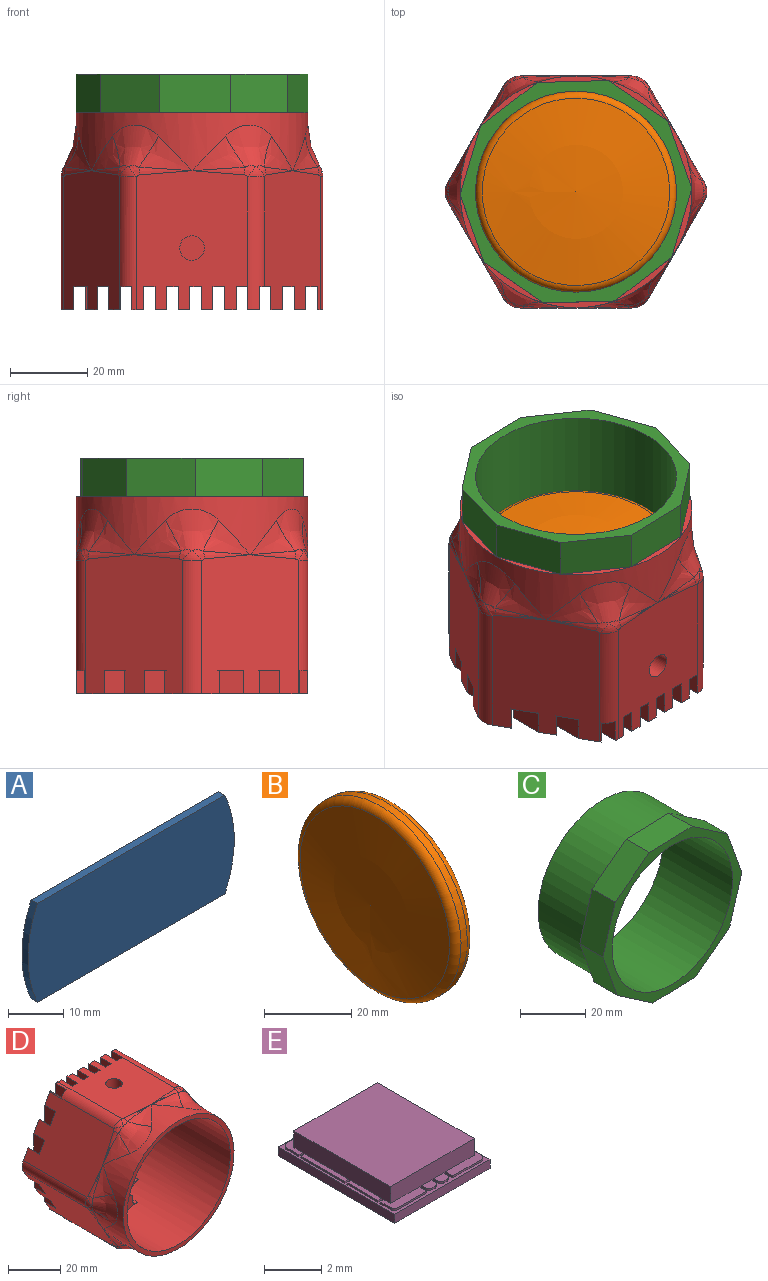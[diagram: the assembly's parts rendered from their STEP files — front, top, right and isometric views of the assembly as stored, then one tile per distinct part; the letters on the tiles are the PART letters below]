
ASSEMBLY  parts=5 mates=4
PART A: 6 faces, bbox 53x1.6x22 mm
  f0: plane 48.22x1.6mm, normal (0,0,1), area 77.1mm2, adj f1,f3,f4,f5
  f1: cylinder r=26.5mm len=22mm, axis (0,1,0), area 36.3mm2, adj f0,f2,f4,f5
  f2: plane 48.22x1.6mm, normal (0,0,-1), area 77.1mm2, adj f1,f3,f4,f5
  f3: cylinder r=26.5mm len=22mm, axis (0,1,0), area 36.3mm2, adj f0,f2,f4,f5
  f4: plane 53x22mm, normal (0,-1,0), area 1131.6mm2, adj f0,f1,f2,f3
  f5: plane 53x22mm, normal (0,1,0), area 1131.6mm2, adj f0,f1,f2,f3
PART B: 5 faces, bbox 11.1x56.3x56.3 mm
  f0: torus R=24mm, axis (1,0,0), area 463.2mm2, adj f1,f4
  f1: cylinder r=26mm len=52mm, axis (1,0,0), area 326.7mm2, adj f0,f2
  f2: torus R=24mm, axis (1,0,0), area 419.7mm2, adj f1,f3
  f3: sphere r=84.13mm, area 1929.7mm2, adj f2
  f4: sphere r=190.83mm, area 1852.7mm2, adj f0
PART C: 15 faces, bbox 60x30x57.5 mm
  f0: cylinder r=28mm len=56mm, axis (0,1,0), area 3518.6mm2, adj f3,f14
  f1: cylinder r=26mm len=52mm, axis (0,1,0), area 4900.9mm2, adj f2,f3
  f2: plane 59.98x57.54mm, normal (0,-1,0), area 521.3mm2, adj f1,f4,f5,f6,f7,f8,f9,f10
  f3: plane 56x56mm, normal (0,1,0), area 339.3mm2, adj f0,f1
  f4: plane 17.78x10mm, normal (0.96,0,-0.28), area 185.4mm2, adj f2,f5,f13,f14
  f5: plane 17.47x10mm, normal (0.94,0,0.33), area 185.4mm2, adj f2,f4,f6,f14
  f6: plane 15.29x10.49mm, normal (0.57,0,0.82), area 185.4mm2, adj f2,f5,f7,f14
  f7: plane 18.53x10mm, normal (-0.03,0,1), area 185.4mm2, adj f2,f6,f8,f14
  f8: plane 14.7x11.3mm, normal (-0.61,0,0.79), area 185.4mm2, adj f2,f7,f9,f14
  f9: plane 17.78x10mm, normal (-0.96,0,0.28), area 185.4mm2, adj f2,f8,f10,f14
  f10: plane 17.47x10mm, normal (-0.94,0,-0.33), area 185.4mm2, adj f2,f9,f11,f14
  f11: plane 15.29x10.49mm, normal (-0.57,0,-0.82), area 185.4mm2, adj f2,f10,f12,f14
  f12: plane 18.53x10mm, normal (0.03,0,-1), area 185.4mm2, adj f2,f11,f13,f14
  f13: plane 14.7x11.3mm, normal (0.61,0,-0.79), area 185.4mm2, adj f2,f4,f12,f14
  f14: plane 59.98x57.54mm, normal (0,1,0), area 182mm2, adj f0,f4,f5,f6,f7,f8,f9,f10
PART D: 168 faces, bbox 72x51.3x64.5 mm
  f0: plane 54.08x30.15mm, normal (0,-1,0), area 1184.2mm2, adj f7,f94,f95,f144,f145,f146,f148,f149
  f1: plane 36.12x25.12mm, normal (-0.87,0,0.5), area 950.7mm2, adj f2,f6,f10,f80,f81,f88,f89,f90
  f2: cylinder r=5mm len=34.46mm, axis (0,1,0), area 180.5mm2, adj f1,f3,f81,f133
  f3: plane 36.12x25.12mm, normal (-0.87,0,-0.5), area 943.5mm2, adj f2,f10,f22,f78,f79,f80,f81,f83
  f4: cylinder r=30mm len=60mm, axis (0,1,0), area 1608.3mm2, adj f8,f96,f97,f98,f99,f100,f101,f102
  f5: plane 36.02x28.89mm, normal (0,0,1), area 901mm2, adj f6,f10,f11,f14,f15,f16,f21,f34
  f6: cylinder r=5mm len=34.46mm, axis (0,1,0), area 158.1mm2, adj f1,f5,f10,f48,f49,f86,f89,f138
  f7: cylinder r=28mm len=56mm, axis (0,1,0), area 6969.1mm2, adj f0,f8,f9,f17,f147,f151,f154,f155
  f8: plane 60x60mm, normal (0,-1,0), area 364.4mm2, adj f4,f7
  f9: plane 47.82x16mm, normal (0,-1,0), area 496.6mm2, adj f7,f25,f94,f162,f163
  f10: plane 60x21mm, normal (0,1,0), area 569.1mm2, adj f1,f3,f5,f6,f19,f22,f25,f44
  f11: plane 60x11.57mm, normal (0,1,0), area 381.1mm2, adj f5,f18,f19,f20,f21,f23,f26,f27
  f12: plane 18.04x3mm, normal (0,1,0), area 38.5mm2, adj f18,f20,f55,f58
  f13: plane 38.82x3mm, normal (0,1,0), area 100.9mm2, adj f18,f20,f57,f61
  f14: plane 60x3mm, normal (0,1,0), area 180mm2, adj f5,f19,f41,f43
  f15: plane 60x3mm, normal (0,1,0), area 180mm2, adj f5,f19,f38,f40
  f16: plane 60x3mm, normal (0,1,0), area 180mm2, adj f5,f19,f35,f37
  f17: plane 47.82x16mm, normal (0,-1,0), area 476mm2, adj f7,f26,f27,f28,f29,f30,f31,f32
  f18: plane 36.33x25.33mm, normal (0.87,0,0.5), area 930.6mm2, adj f11,f12,f13,f21,f24,f55,f56,f57
  f19: plane 36.02x28.89mm, normal (0,0,-1), area 901mm2, adj f10,f11,f14,f15,f16,f22,f23,f34
  f20: plane 36.09x25.1mm, normal (0.87,0,-0.5), area 930.6mm2, adj f11,f12,f13,f23,f24,f55,f56,f57
  f21: cylinder r=5mm len=34.46mm, axis (0,1,0), area 168.3mm2, adj f5,f11,f18,f50,f53,f54,f143
  f22: cylinder r=5mm len=34.46mm, axis (0,1,0), area 158.1mm2, adj f3,f10,f19,f74,f75,f77,f79,f128
  f23: cylinder r=5mm len=34.46mm, axis (0,1,0), area 168.3mm2, adj f11,f19,f20,f68,f69,f71,f123
  f24: cylinder r=5mm len=34.46mm, axis (0,1,0), area 180.5mm2, adj f18,f20,f56,f118
  f25: cylinder r=5mm len=10mm, axis (0,1,0), area 62.8mm2, adj f9,f10
  f26: plane 3x2mm, normal (0,0,-1), area 6mm2, adj f11,f17,f27,f33
  f27: cylinder r=1mm len=2mm, axis (0,1,0), area 3.1mm2, adj f11,f17,f26,f28
  f28: plane 18x2mm, normal (-1,0,0), area 36mm2, adj f11,f17,f27,f29
  f29: cylinder r=1mm len=2mm, axis (0,1,0), area 3.1mm2, adj f11,f17,f28,f30
  f30: plane 3x2mm, normal (0,0,1), area 6mm2, adj f11,f17,f29,f31
  f31: cylinder r=1mm len=2mm, axis (0,1,0), area 3.1mm2, adj f11,f17,f30,f32
  f32: plane 18x2mm, normal (1,0,0), area 36mm2, adj f11,f17,f31,f33
  f33: cylinder r=1mm len=2mm, axis (0,1,0), area 3.1mm2, adj f11,f17,f26,f32
  f34: plane 60x6mm, normal (1,0,0), area 360mm2, adj f5,f11,f19,f36
  f35: plane 60x6mm, normal (-1,0,0), area 360mm2, adj f5,f16,f19,f36
  f36: plane 60x3mm, normal (0,1,0), area 180mm2, adj f5,f19,f34,f35
  f37: plane 60x6mm, normal (1,0,0), area 360mm2, adj f5,f16,f19,f39
  f38: plane 60x6mm, normal (-1,0,0), area 360mm2, adj f5,f15,f19,f39
  f39: plane 60x3mm, normal (0,1,0), area 180mm2, adj f5,f19,f37,f38
  f40: plane 60x6mm, normal (1,0,0), area 360mm2, adj f5,f15,f19,f42
  f41: plane 60x6mm, normal (-1,0,0), area 360mm2, adj f5,f14,f19,f42
  f42: plane 60x3mm, normal (0,1,0), area 180mm2, adj f5,f19,f40,f41
  f43: plane 60x6mm, normal (1,0,0), area 360mm2, adj f5,f14,f19,f45
  f44: plane 60x6mm, normal (-1,0,0), area 360mm2, adj f5,f10,f19,f45
  f45: plane 60x3mm, normal (0,1,0), area 180mm2, adj f5,f19,f43,f44
  f46: plane 27.04x6mm, normal (1,0,0), area 162.3mm2, adj f5,f10,f47,f49
  f47: cylinder r=8mm len=6mm, axis (0,-1,0), area 29mm2, adj f10,f46,f48,f49
  f48: plane 23.21x6mm, normal (-1,0,0), area 139.3mm2, adj f6,f10,f47,f49
  f49: plane 27.04x3mm, normal (0,1,0), area 74.4mm2, adj f5,f6,f46,f47,f48
  f50: plane 16x6mm, normal (1,0,0), area 96mm2, adj f11,f21,f51,f54
  f51: plane 6x1.43mm, normal (0,0,-1), area 8.6mm2, adj f11,f50,f52,f54
  f52: cylinder r=4mm len=6mm, axis (0,-1,0), area 9.7mm2, adj f11,f51,f53,f54
  f53: plane 17.32x6mm, normal (-1,0,0), area 103.9mm2, adj f11,f21,f52,f54
  f54: plane 17.32x3mm, normal (0,1,0), area 50.2mm2, adj f21,f50,f51,f52,f53
  f55: plane 7.65x6mm, normal (-1,0,0), area 45.9mm2, adj f12,f18,f20,f56
  f56: plane 7.65x1.43mm, normal (0,1,0), area 7.1mm2, adj f18,f20,f24,f55
  f57: plane 28.43x6mm, normal (-1,0,0), area 170.6mm2, adj f13,f18,f20,f59
  f58: plane 18.04x6mm, normal (1,0,0), area 108.2mm2, adj f12,f18,f20,f59
  f59: plane 28.43x3mm, normal (0,1,0), area 69.7mm2, adj f18,f20,f57,f58
  f60: plane 11.87x6mm, normal (-1,0,0), area 71.2mm2, adj f11,f18,f65,f66
  f61: plane 38.82x6mm, normal (1,0,0), area 232.9mm2, adj f13,f18,f20,f66
  f62: plane 11.87x6mm, normal (-1,0,0), area 71.2mm2, adj f11,f20,f63,f66
  f63: cylinder r=4mm len=6mm, axis (0,-1,0), area 28.9mm2, adj f11,f62,f64,f66
  f64: plane 18x6mm, normal (-1,0,0), area 108mm2, adj f11,f63,f65,f66
  f65: cylinder r=4mm len=6mm, axis (0,-1,0), area 28.9mm2, adj f11,f60,f64,f66
  f66: plane 49.22x3mm, normal (0,1,0), area 72mm2, adj f18,f20,f60,f61,f62,f63,f64,f65
  f67: plane 6x1.43mm, normal (0,0,1), area 8.6mm2, adj f11,f68,f70,f71
  f68: plane 16x6mm, normal (1,0,0), area 96mm2, adj f11,f23,f67,f71
  f69: plane 17.32x6mm, normal (-1,0,0), area 103.9mm2, adj f11,f23,f70,f71
  f70: cylinder r=4mm len=6mm, axis (0,-1,0), area 9.7mm2, adj f11,f67,f69,f71
  f71: plane 17.32x3mm, normal (0,1,0), area 50.2mm2, adj f23,f67,f68,f69,f70
  f72: cylinder r=8mm len=6mm, axis (0,-1,0), area 29mm2, adj f10,f73,f74,f75
  f73: plane 27.04x6mm, normal (1,0,0), area 162.3mm2, adj f10,f19,f72,f75
  f74: plane 23.21x6mm, normal (-1,0,0), area 139.3mm2, adj f10,f22,f72,f75
  f75: plane 27.04x3mm, normal (0,1,0), area 74.4mm2, adj f19,f22,f72,f73,f74
  f76: cylinder r=8mm len=6mm, axis (0,-1,0), area 18.1mm2, adj f10,f77,f78,f79
  f77: plane 19.94x6mm, normal (1,0,0), area 119.7mm2, adj f10,f22,f76,f79
  f78: plane 14.8x6mm, normal (-1,0,0), area 88.8mm2, adj f3,f10,f76,f79
  f79: plane 19.97x3mm, normal (0,1,0), area 51.9mm2, adj f3,f22,f76,f77,f78
  f80: plane 14.12x6mm, normal (1,0,0), area 84.7mm2, adj f1,f3,f10,f81
  f81: plane 14.12x3.3mm, normal (0,1,0), area 27.4mm2, adj f1,f2,f3,f80
  f82: cylinder r=8mm len=6mm, axis (0,-1,0), area 21.6mm2, adj f10,f83,f84,f85
  f83: plane 10.88x6mm, normal (1,0,0), area 65.3mm2, adj f3,f10,f82,f85
  f84: plane 9.36x6mm, normal (-1,0,0), area 56.2mm2, adj f3,f10,f82,f85
  f85: plane 13.52x2.4mm, normal (0,1,0), area 23.9mm2, adj f3,f82,f83,f84
  f86: plane 19.94x6mm, normal (1,0,0), area 119.7mm2, adj f6,f10,f87,f89
  f87: cylinder r=8mm len=6mm, axis (0,-1,0), area 18.1mm2, adj f10,f86,f88,f89
  f88: plane 14.8x6mm, normal (-1,0,0), area 88.8mm2, adj f1,f10,f87,f89
  f89: plane 19.97x3mm, normal (0,1,0), area 51.9mm2, adj f1,f6,f86,f87,f88
  f90: plane 10.88x6mm, normal (1,0,0), area 65.3mm2, adj f1,f10,f91,f93
  f91: cylinder r=8mm len=6mm, axis (0,-1,0), area 30.4mm2, adj f10,f90,f92,f93
  f92: plane 9.66x6mm, normal (-1,0,0), area 57.9mm2, adj f1,f10,f91,f93
  f93: plane 14.85x3mm, normal (0,1,0), area 29.5mm2, adj f1,f90,f91,f92
  f94: plane 43.82x6mm, normal (-1,0,0), area 262.9mm2, adj f0,f9,f162,f163
  f95: plane 43.82x6mm, normal (1,0,0), area 262.9mm2, adj f0,f17,f164,f165
  f96: bspline ~17.09x12.09mm, area 38.5mm2, adj f4,f97,f115
  f97: bspline ~14.81x11.82mm, area 108.6mm2, adj f4,f96,f98,f116,f117
  f98: bspline ~17.09x12.09mm, area 38.5mm2, adj f4,f97,f114
  f99: bspline ~17.09x12.09mm, area 38.5mm2, adj f4,f100,f120
  f100: bspline ~12.76x11.82mm, area 108.6mm2, adj f4,f99,f101,f121,f122
  f101: bspline ~19.74x12.09mm, area 38.5mm2, adj f4,f100,f119
  f102: bspline ~19.74x12.09mm, area 38.5mm2, adj f4,f103,f125
  f103: bspline ~12.9x11.82mm, area 108.6mm2, adj f4,f102,f104,f126,f127
  f104: bspline ~17.09x12.09mm, area 38.5mm2, adj f4,f103,f124
  f105: bspline ~17.09x12.09mm, area 38.5mm2, adj f4,f106,f130
  f106: bspline ~14.81x11.82mm, area 108.6mm2, adj f4,f105,f107,f131,f132
  f107: bspline ~17.09x12.09mm, area 38.5mm2, adj f4,f106,f129
  f108: bspline ~17.09x12.09mm, area 38.5mm2, adj f4,f109,f135
  f109: bspline ~12.76x11.82mm, area 108.6mm2, adj f4,f108,f110,f136,f137
  f110: bspline ~19.74x12.09mm, area 38.5mm2, adj f4,f109,f134
  f111: bspline ~19.74x12.09mm, area 38.5mm2, adj f4,f112,f140
  f112: bspline ~12.9x11.82mm, area 108.6mm2, adj f4,f111,f113,f141,f142
  f113: bspline ~17.09x12.09mm, area 38.5mm2, adj f4,f112,f139
  f114: bspline ~15.78x8.85mm, area 9.4mm2, adj f20,f98,f116
  f115: bspline ~13.29x7.48mm, area 9.4mm2, adj f18,f96,f117
  f116: bspline ~3.35x2.86mm, area 5.3mm2, adj f20,f97,f114,f118
  f117: bspline ~3.57x2.93mm, area 5.3mm2, adj f18,f97,f115,f118
  f118: sphere r=5mm, area 11.1mm2, adj f24,f116,f117
  f119: bspline ~17.8x2.59mm, area 9.4mm2, adj f19,f101,f121
  f120: bspline ~12.95x7.97mm, area 9.4mm2, adj f20,f99,f122
  f121: bspline ~3.07x2.86mm, area 5.3mm2, adj f19,f100,f119,f123
  f122: bspline ~2.93x2.91mm, area 5.3mm2, adj f20,f100,f120,f123
  f123: sphere r=5mm, area 11mm2, adj f23,f121,f122
  f124: bspline ~15.32x9.53mm, area 9.4mm2, adj f3,f104,f126
  f125: bspline ~15.04x2.2mm, area 9.4mm2, adj f19,f102,f127
  f126: bspline ~2.86x2.73mm, area 5.4mm2, adj f3,f103,f124,f128
  f127: bspline ~3.28x2.93mm, area 5.3mm2, adj f19,f103,f125,f128
  f128: sphere r=5mm, area 11mm2, adj f22,f126,f127
  f129: bspline ~15.78x8.85mm, area 9.4mm2, adj f1,f107,f131
  f130: bspline ~13.29x7.48mm, area 9.4mm2, adj f3,f105,f132
  f131: bspline ~3.35x2.86mm, area 5.3mm2, adj f1,f106,f129,f133
  f132: bspline ~3.57x2.93mm, area 5.3mm2, adj f3,f106,f130,f133
  f133: sphere r=5mm, area 7.8mm2, adj f2,f131,f132
  f134: bspline ~17.8x2.59mm, area 9.4mm2, adj f5,f110,f136
  f135: bspline ~12.95x7.97mm, area 9.4mm2, adj f1,f108,f137
  f136: bspline ~3.07x2.86mm, area 5.3mm2, adj f5,f109,f134,f138
  f137: bspline ~2.93x2.91mm, area 5.3mm2, adj f1,f109,f135,f138
  f138: sphere r=5mm, area 7.7mm2, adj f6,f136,f137
  f139: bspline ~15.32x9.53mm, area 9.4mm2, adj f18,f113,f141
  f140: bspline ~15.04x2.2mm, area 9.4mm2, adj f5,f111,f142
  f141: bspline ~2.86x2.73mm, area 5.4mm2, adj f18,f112,f139,f143
  f142: bspline ~3.28x2.93mm, area 5.3mm2, adj f5,f112,f140,f143
  f143: sphere r=5mm, area 7.7mm2, adj f21,f141,f142
  f144: plane 7x1.49mm, normal (-1,0,0), area 10.4mm2, adj f0,f147,f154,f157
  f145: plane 7x1.49mm, normal (1,0,0), area 10.4mm2, adj f0,f147,f155,f156
  f146: plane 7x6mm, normal (0,0,1), area 42mm2, adj f0,f147,f156,f157
  f147: plane 15.08x6.45mm, normal (0,-1,0), area 64.2mm2, adj f7,f144,f145,f146,f154,f155,f156,f157
  f148: plane 7x1.49mm, normal (-1,0,0), area 10.4mm2, adj f0,f151,f160,f161
  f149: plane 7x6mm, normal (0,0,-1), area 42mm2, adj f0,f151,f159,f160
  f150: plane 7x1.49mm, normal (1,0,0), area 10.4mm2, adj f0,f151,f158,f159
  f151: plane 15.08x6.45mm, normal (0,-1,0), area 64.2mm2, adj f7,f148,f149,f150,f158,f159,f160,f161
  f152: cylinder r=3.17mm len=8mm, axis (0,0,-1), area 159.6mm2, adj f19,f153
  f153: plane 6.35x6.35mm, normal (0,0,-1), area 31.7mm2, adj f152
  f154: cylinder r=2mm len=7mm, axis (0,1,0), area 25.8mm2, adj f0,f7,f144,f147
  f155: cylinder r=2mm len=7mm, axis (0,1,0), area 25.8mm2, adj f0,f7,f145,f147
  f156: cylinder r=2mm len=7mm, axis (0,1,0), area 22mm2, adj f0,f145,f146,f147
  f157: cylinder r=2mm len=7mm, axis (0,1,0), area 22mm2, adj f0,f144,f146,f147
  f158: cylinder r=2mm len=7mm, axis (0,1,0), area 25.8mm2, adj f0,f7,f150,f151
  f159: cylinder r=2mm len=7mm, axis (0,1,0), area 22mm2, adj f0,f149,f150,f151
  f160: cylinder r=2mm len=7mm, axis (0,1,0), area 22mm2, adj f0,f148,f149,f151
  f161: cylinder r=2mm len=7mm, axis (0,1,0), area 25.8mm2, adj f0,f7,f148,f151
  f162: cylinder r=2mm len=6mm, axis (0,1,0), area 25.7mm2, adj f0,f7,f9,f94
  f163: cylinder r=2mm len=6mm, axis (0,1,0), area 25.7mm2, adj f0,f7,f9,f94
  f164: cylinder r=2mm len=6mm, axis (0,1,0), area 25.7mm2, adj f0,f7,f17,f95
  f165: cylinder r=2mm len=6mm, axis (0,1,0), area 25.7mm2, adj f0,f7,f17,f95
  f166: cylinder r=3.17mm len=8mm, axis (0,0,1), area 159.6mm2, adj f5,f167
  f167: plane 6.35x6.35mm, normal (0,0,1), area 31.7mm2, adj f166
PART E: 120 faces, bbox 4.7x5.8x1.3 mm
  f0: plane 4.76x4.11mm, normal (0,0,1), area 19.6mm2, adj f1,f2,f3,f4
  f1: plane 4.76x0.79mm, normal (1,0,0), area 3.4mm2, adj f0,f2,f4,f5,f6,f7,f8,f9
  f2: plane 4.11x0.79mm, normal (0,-1,0), area 2.9mm2, adj f0,f1,f3,f11,f12,f13,f14,f15
  f3: plane 4.76x0.79mm, normal (-1,0,0), area 3.4mm2, adj f0,f2,f4,f20,f21,f22,f23,f24
  f4: plane 4.11x0.79mm, normal (0,1,0), area 2.9mm2, adj f0,f1,f3,f5,f29,f30,f31,f32
  f5: plane 2.32x0.45mm, normal (0,0,1), area 0.5mm2, adj f1,f4,f6,f37,f38,f39,f40
  f6: plane 0.19x0.08mm, normal (0,-1,0), area 0mm2, adj f1,f5,f40,f67
  f7: plane 0.19x0.08mm, normal (0,1,0), area 0mm2, adj f1,f8,f41,f67
  f8: plane 2.17x0.19mm, normal (0,0,1), area 0.4mm2, adj f1,f7,f9,f41
  f9: plane 0.19x0.08mm, normal (0,-1,0), area 0mm2, adj f1,f8,f41,f67
  f10: plane 0.19x0.08mm, normal (0,1,0), area 0mm2, adj f1,f11,f42,f67
  f11: plane 1.6x0.79mm, normal (0,0,1), area 0.6mm2, adj f1,f2,f10,f12,f42,f43,f44
  f12: plane 0.36x0.08mm, normal (-1,0,0), area 0mm2, adj f2,f11,f44,f67
  f13: plane 0.16x0.08mm, normal (1,0,0), area 0mm2, adj f2,f14,f45,f67
  f14: plane 0.5x0.36mm, normal (0,0,1), area 0.2mm2, adj f2,f13,f15,f45,f46,f47
  f15: plane 0.16x0.08mm, normal (-1,0,0), area 0mm2, adj f2,f14,f47,f67
  f16: plane 0.16x0.08mm, normal (1,0,0), area 0mm2, adj f2,f17,f48,f67
  f17: plane 0.5x0.36mm, normal (0,0,1), area 0.2mm2, adj f2,f16,f18,f48,f49,f50
  f18: plane 0.16x0.08mm, normal (-1,0,0), area 0mm2, adj f2,f17,f50,f67
  f19: plane 0.36x0.08mm, normal (1,0,0), area 0mm2, adj f2,f20,f51,f67
  f20: plane 1.6x0.7mm, normal (0,0,1), area 0.6mm2, adj f2,f3,f19,f28,f51,f52,f53
  f21: plane 0.19x0.08mm, normal (0,-1,0), area 0mm2, adj f3,f22,f54,f67
  f22: plane 1.52x0.19mm, normal (0,0,1), area 0.3mm2, adj f3,f21,f23,f54
  f23: plane 0.19x0.08mm, normal (0,1,0), area 0mm2, adj f3,f22,f54,f67
  f24: plane 0.19x0.08mm, normal (0,-1,0), area 0mm2, adj f3,f25,f55,f67
  f25: plane 2.17x0.19mm, normal (0,0,1), area 0.4mm2, adj f3,f24,f26,f55
  f26: plane 0.19x0.08mm, normal (0,1,0), area 0mm2, adj f3,f25,f55,f67
  f27: plane 0.19x0.08mm, normal (0,-1,0), area 0mm2, adj f3,f29,f56,f67
  f28: plane 0.19x0.08mm, normal (0,1,0), area 0mm2, adj f3,f20,f53,f67
  f29: plane 1.6x0.79mm, normal (0,0,1), area 0.6mm2, adj f3,f4,f27,f30,f56,f57,f58
  f30: plane 0.36x0.08mm, normal (1,0,0), area 0mm2, adj f4,f29,f58,f67
  f31: plane 0.16x0.08mm, normal (-1,0,0), area 0mm2, adj f4,f32,f59,f67
  f32: plane 0.5x0.36mm, normal (0,0,1), area 0.2mm2, adj f4,f31,f33,f59,f60,f61
  f33: plane 0.16x0.08mm, normal (1,0,0), area 0mm2, adj f4,f32,f61,f67
  f34: plane 0.16x0.08mm, normal (-1,0,0), area 0mm2, adj f4,f35,f62,f67
  f35: plane 1.65x0.36mm, normal (0,0,1), area 0.3mm2, adj f4,f34,f36,f62,f63,f64,f65,f66
  f36: plane 0.11x0.08mm, normal (1,0,0), area 0mm2, adj f4,f35,f66,f67
  f37: plane 0.36x0.08mm, normal (-1,0,0), area 0mm2, adj f4,f5,f38,f67
  f38: plane 0.25x0.08mm, normal (0,1,0), area 0mm2, adj f5,f37,f39,f67
  f39: cylinder r=0.2mm len=0.2mm, axis (0,0,-1), area 0mm2, adj f5,f38,f40,f67
  f40: plane 2.12x0.08mm, normal (1,0,0), area 0.2mm2, adj f5,f6,f39,f67
  f41: plane 2.17x0.08mm, normal (1,0,0), area 0.2mm2, adj f7,f8,f9,f67
  f42: plane 0.59x0.08mm, normal (1,0,0), area 0mm2, adj f10,f11,f43,f67
  f43: cylinder r=0.2mm len=0.2mm, axis (0,0,-1), area 0mm2, adj f11,f42,f44,f67
  f44: plane 1.4x0.08mm, normal (0,-1,0), area 0.1mm2, adj f11,f12,f43,f67
  f45: cylinder r=0.2mm len=0.2mm, axis (0,0,-1), area 0mm2, adj f13,f14,f46,f67
  f46: plane 0.1x0.08mm, normal (0,-1,0), area 0mm2, adj f14,f45,f47,f67
  f47: cylinder r=0.2mm len=0.2mm, axis (0,0,-1), area 0mm2, adj f14,f15,f46,f67
  f48: cylinder r=0.2mm len=0.2mm, axis (0,0,-1), area 0mm2, adj f16,f17,f49,f67
  f49: plane 0.1x0.08mm, normal (0,-1,0), area 0mm2, adj f17,f48,f50,f67
  f50: cylinder r=0.2mm len=0.2mm, axis (0,0,-1), area 0mm2, adj f17,f18,f49,f67
  f51: plane 1.4x0.08mm, normal (0,-1,0), area 0.1mm2, adj f19,f20,f52,f67
  f52: cylinder r=0.2mm len=0.2mm, axis (0,0,-1), area 0mm2, adj f20,f51,f53,f67
  f53: plane 0.5x0.08mm, normal (-1,0,0), area 0mm2, adj f20,f28,f52,f67
  f54: plane 1.52x0.08mm, normal (-1,0,0), area 0.1mm2, adj f21,f22,f23,f67
  f55: plane 2.17x0.08mm, normal (-1,0,0), area 0.2mm2, adj f24,f25,f26,f67
  f56: plane 0.59x0.08mm, normal (-1,0,0), area 0mm2, adj f27,f29,f57,f67
  f57: cylinder r=0.2mm len=0.2mm, axis (0,0,-1), area 0mm2, adj f29,f56,f58,f67
  f58: plane 1.4x0.08mm, normal (0,1,0), area 0.1mm2, adj f29,f30,f57,f67
  f59: cylinder r=0.2mm len=0.2mm, axis (0,0,-1), area 0mm2, adj f31,f32,f60,f67
  f60: plane 0.1x0.08mm, normal (0,1,0), area 0mm2, adj f32,f59,f61,f67
  f61: cylinder r=0.2mm len=0.2mm, axis (0,0,-1), area 0mm2, adj f32,f33,f60,f67
  f62: cylinder r=0.2mm len=0.2mm, axis (0,0,-1), area 0mm2, adj f34,f35,f63,f67
  f63: plane 0.1x0.08mm, normal (0,1,0), area 0mm2, adj f35,f62,f64,f67
  f64: cylinder r=0.2mm len=0.2mm, axis (0,0,-1), area 0mm2, adj f35,f63,f65,f67
  f65: plane 0.08x0.05mm, normal (1,0,0), area 0mm2, adj f35,f64,f66,f67
  f66: plane 1.15x0.08mm, normal (0,1,0), area 0.1mm2, adj f35,f36,f65,f67
  f67: plane 5.75x4.68mm, normal (0,0,1), area 3.1mm2, adj f1,f2,f3,f4,f6,f7,f9,f10
  f68: plane 4.68x0.38mm, normal (0,-1,0), area 1.8mm2, adj f67,f69,f71,f72
  f69: plane 5.75x0.38mm, normal (-1,0,0), area 2.2mm2, adj f67,f68,f70,f72
  f70: plane 4.68x0.38mm, normal (0,1,0), area 1.8mm2, adj f67,f69,f71,f72
  f71: plane 5.75x0.38mm, normal (1,0,0), area 2.2mm2, adj f67,f68,f70,f72
  f72: plane 5.75x4.68mm, normal (0,0,-1), area 7.7mm2, adj f68,f69,f70,f71,f73,f74,f75,f76
  f73: plane 0.77x0.08mm, normal (0,1,0), area 0.1mm2, adj f72,f74,f76,f111
  f74: plane 0.75x0.08mm, normal (1,0,0), area 0.1mm2, adj f72,f73,f75,f111
  f75: plane 0.77x0.08mm, normal (0,-1,0), area 0.1mm2, adj f72,f74,f76,f111
  f76: plane 0.75x0.08mm, normal (-1,0,0), area 0.1mm2, adj f72,f73,f75,f111
  f77: plane 0.87x0.08mm, normal (0,1,0), area 0.1mm2, adj f72,f78,f80,f112
  f78: plane 0.75x0.08mm, normal (1,0,0), area 0.1mm2, adj f72,f77,f79,f112
  f79: plane 0.87x0.08mm, normal (0,-1,0), area 0.1mm2, adj f72,f78,f80,f112
  f80: plane 0.75x0.08mm, normal (-1,0,0), area 0.1mm2, adj f72,f77,f79,f112
  f81: plane 0.75x0.08mm, normal (-1,0,0), area 0.1mm2, adj f72,f82,f84,f113
  f82: plane 0.87x0.08mm, normal (0,1,0), area 0.1mm2, adj f72,f81,f83,f113
  f83: plane 0.75x0.08mm, normal (1,0,0), area 0.1mm2, adj f72,f82,f84,f113
  f84: plane 0.87x0.08mm, normal (0,-1,0), area 0.1mm2, adj f72,f81,f83,f113
  f85: plane 0.75x0.08mm, normal (-1,0,0), area 0.1mm2, adj f72,f86,f88,f114
  f86: plane 0.77x0.08mm, normal (0,1,0), area 0.1mm2, adj f72,f85,f87,f114
  f87: plane 0.75x0.08mm, normal (1,0,0), area 0.1mm2, adj f72,f86,f88,f114
  f88: plane 0.77x0.08mm, normal (0,-1,0), area 0.1mm2, adj f72,f85,f87,f114
  f89: cylinder r=0.4mm len=0.8mm, axis (0,0,1), area 0.1mm2, adj f72,f90,f94,f115
  f90: plane 1.23x0.08mm, normal (1,0,0), area 0.1mm2, adj f72,f89,f91,f115
  f91: plane 4.48x0.08mm, normal (0,-1,0), area 0.4mm2, adj f72,f90,f92,f115
  f92: plane 3.25x0.08mm, normal (-1,0,0), area 0.3mm2, adj f72,f91,f93,f115
  f93: plane 4.48x0.08mm, normal (0,1,0), area 0.4mm2, adj f72,f92,f94,f115
  f94: plane 1.23x0.08mm, normal (1,0,0), area 0.1mm2, adj f72,f89,f93,f115
  f95: plane 0.77x0.08mm, normal (0,-1,0), area 0.1mm2, adj f72,f96,f98,f116
  f96: plane 0.75x0.08mm, normal (-1,0,0), area 0.1mm2, adj f72,f95,f97,f116
  f97: plane 0.77x0.08mm, normal (0,1,0), area 0.1mm2, adj f72,f96,f98,f116
  f98: plane 0.75x0.08mm, normal (1,0,0), area 0.1mm2, adj f72,f95,f97,f116
  f99: plane 0.87x0.08mm, normal (0,-1,0), area 0.1mm2, adj f72,f100,f102,f117
  f100: plane 0.75x0.08mm, normal (-1,0,0), area 0.1mm2, adj f72,f99,f101,f117
  f101: plane 0.87x0.08mm, normal (0,1,0), area 0.1mm2, adj f72,f100,f102,f117
  f102: plane 0.75x0.08mm, normal (1,0,0), area 0.1mm2, adj f72,f99,f101,f117
  f103: plane 0.87x0.08mm, normal (0,1,0), area 0.1mm2, adj f72,f104,f106,f118
  f104: plane 0.75x0.08mm, normal (1,0,0), area 0.1mm2, adj f72,f103,f105,f118
  f105: plane 0.87x0.08mm, normal (0,-1,0), area 0.1mm2, adj f72,f104,f106,f118
  f106: plane 0.75x0.08mm, normal (-1,0,0), area 0.1mm2, adj f72,f103,f105,f118
  f107: plane 0.75x0.08mm, normal (1,0,0), area 0.1mm2, adj f72,f108,f110,f119
  f108: plane 0.77x0.08mm, normal (0,-1,0), area 0.1mm2, adj f72,f107,f109,f119
  f109: plane 0.75x0.08mm, normal (-1,0,0), area 0.1mm2, adj f72,f108,f110,f119
  f110: plane 0.77x0.08mm, normal (0,1,0), area 0.1mm2, adj f72,f107,f109,f119
  f111: plane 0.77x0.75mm, normal (0,0,-1), area 0.6mm2, adj f73,f74,f75,f76
  f112: plane 0.87x0.75mm, normal (0,0,-1), area 0.7mm2, adj f77,f78,f79,f80
  f113: plane 0.87x0.75mm, normal (0,0,-1), area 0.7mm2, adj f81,f82,f83,f84
  f114: plane 0.77x0.75mm, normal (0,0,-1), area 0.6mm2, adj f85,f86,f87,f88
  f115: plane 4.48x3.25mm, normal (0,0,-1), area 14.3mm2, adj f89,f90,f91,f92,f93,f94
  f116: plane 0.77x0.75mm, normal (0,0,-1), area 0.6mm2, adj f95,f96,f97,f98
  f117: plane 0.87x0.75mm, normal (0,0,-1), area 0.7mm2, adj f99,f100,f101,f102
  f118: plane 0.87x0.75mm, normal (0,0,-1), area 0.7mm2, adj f103,f104,f105,f106
  f119: plane 0.77x0.75mm, normal (0,0,-1), area 0.6mm2, adj f107,f108,f109,f110
PLACE A rot(axis=(-1,0,0),90deg) t=(-52.52,-2.68,-33.97)mm
PLACE B rot(axis=(0,1,0),90deg) t=(-52.52,-13.68,-7.89)mm
PLACE C rot(axis=(-1,0,0),90deg) t=(-52.52,-13.68,-16.97)mm
PLACE D rot(axis=(-1,0,0),90deg) t=(-52.52,-13.68,-41.97)mm
PLACE E t=(-52.48,-13.68,-31.12)mm
MATE fastened A.f1 <-> D.f7  axis (0,0,-1) through (-52.52,-13.68,-33.97)mm
MATE fastened C.f1 <-> B.f0  axis (0,0,-1) through (-52.52,-13.68,-16.97)mm
MATE fastened D.f7 <-> C.f1  axis (0,0,1) through (-52.52,-13.68,3.03)mm
MATE fastened A.f1 <-> E.f115  axis (0,0,1) through (-52.52,-13.68,-32.37)mm
